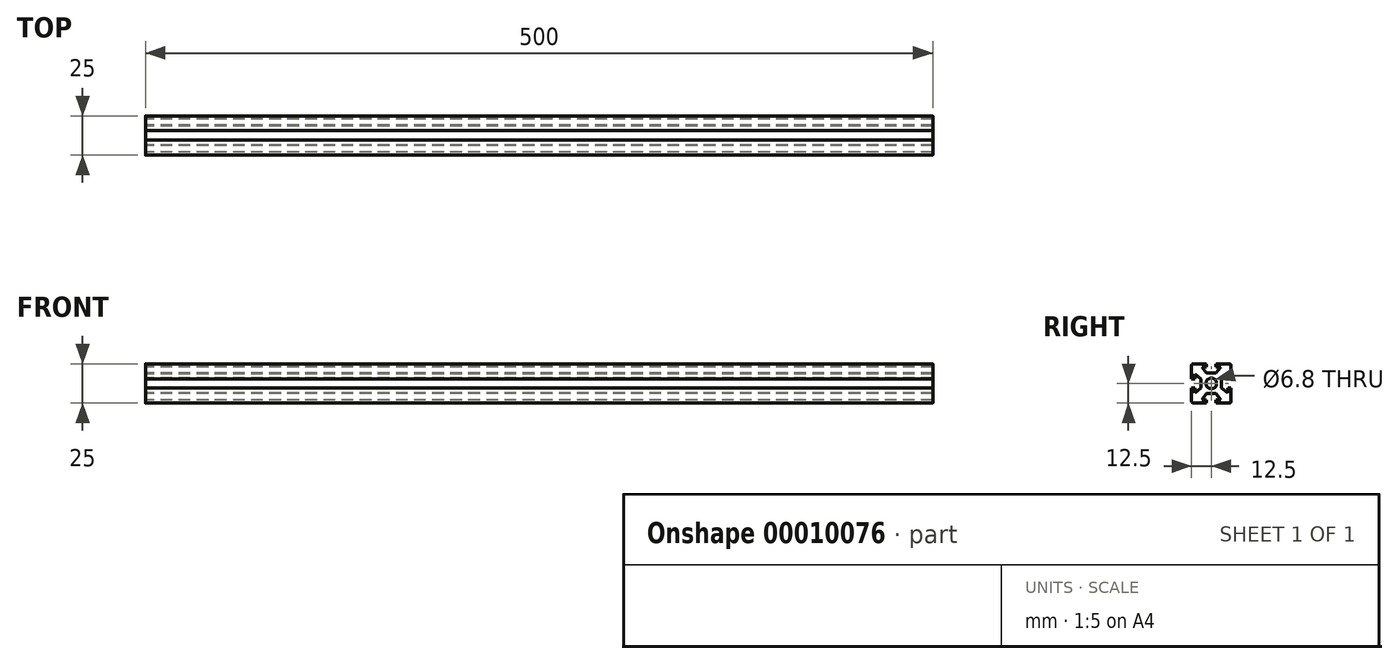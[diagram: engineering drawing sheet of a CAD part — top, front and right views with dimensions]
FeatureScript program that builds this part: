
annotation { "Feature Type Name" : "Feature", "Feature Type Description" : "" }
export const myFeature = defineFeature(function(context is Context, id is Id, definition is map)
    precondition{}
    {
        {
            var Q0;
            Q0=qCreatedBy(makeId("Right.planeOp"),FACE);
            var sketch = newSketch(context, id + "F0", { "sketchPlane" : qUnion([Q0])});
            skLineSegment(sketch, "E0", {"start": v(3, -12.5) * mm, "end": v(12.5, -12.5) * mm});
            skLineSegment(sketch, "E1", {"start": v(12.5, -12.5) * mm, "end": v(12.5, -3) * mm});
            skLineSegment(sketch, "E2", {"start": v(12.5, -3) * mm, "end": v(10.5, -3) * mm});
            skLineSegment(sketch, "E3", {"start": v(10.5, -3) * mm, "end": v(10.5, -6) * mm});
            skLineSegment(sketch, "E4", {"start": v(10.5, -6) * mm, "end": v(6.5, -3) * mm});
            skLineSegment(sketch, "E5", {"start": v(6.5, -3) * mm, "end": v(6.5, 3) * mm});
            skLineSegment(sketch, "E6", {"start": v(6.5, 3) * mm, "end": v(10.5, 6) * mm});
            skLineSegment(sketch, "E7", {"start": v(10.5, 6) * mm, "end": v(10.5, 3) * mm});
            skLineSegment(sketch, "E8", {"start": v(10.5, 3) * mm, "end": v(12.5, 3) * mm});
            skLineSegment(sketch, "E9", {"start": v(12.5, 3) * mm, "end": v(12.5, 12.5) * mm});
            skLineSegment(sketch, "E10", {"start": v(12.5, 12.5) * mm, "end": v(3, 12.5) * mm});
            skLineSegment(sketch, "E11", {"start": v(3, 12.5) * mm, "end": v(3, 10.5) * mm});
            skLineSegment(sketch, "E12", {"start": v(3, 10.5) * mm, "end": v(6, 10.5) * mm});
            skLineSegment(sketch, "E13", {"start": v(6, 10.5) * mm, "end": v(3, 6.5) * mm});
            skLineSegment(sketch, "E14", {"start": v(-3, 6.5) * mm, "end": v(-6, 10.5) * mm});
            skLineSegment(sketch, "E15", {"start": v(-6, 10.5) * mm, "end": v(-3, 10.5) * mm});
            skLineSegment(sketch, "E16", {"start": v(-3, 10.5) * mm, "end": v(-3, 12.5) * mm});
            skLineSegment(sketch, "E17", {"start": v(-3, 12.5) * mm, "end": v(-12.5, 12.5) * mm});
            skLineSegment(sketch, "E18", {"start": v(-12.5, 12.5) * mm, "end": v(-12.5, 3) * mm});
            skLineSegment(sketch, "E19", {"start": v(-12.5, 3) * mm, "end": v(-10.5, 3) * mm});
            skLineSegment(sketch, "E20", {"start": v(-10.5, 3) * mm, "end": v(-10.5, 6) * mm});
            skLineSegment(sketch, "E21", {"start": v(-10.5, 6) * mm, "end": v(-6.5, 3) * mm});
            skLineSegment(sketch, "E22", {"start": v(-6.5, 3) * mm, "end": v(-6.5, -3) * mm});
            skLineSegment(sketch, "E23", {"start": v(-6.5, -3) * mm, "end": v(-10.5, -6) * mm});
            skLineSegment(sketch, "E24", {"start": v(-10.5, -6) * mm, "end": v(-10.5, -3) * mm});
            skLineSegment(sketch, "E25", {"start": v(-10.5, -3) * mm, "end": v(-12.5, -3) * mm});
            skLineSegment(sketch, "E26", {"start": v(-12.5, -3) * mm, "end": v(-12.5, -12.5) * mm});
            skLineSegment(sketch, "E27", {"start": v(-12.5, -12.5) * mm, "end": v(-3, -12.5) * mm});
            skLineSegment(sketch, "E28", {"start": v(-3, -12.5) * mm, "end": v(-3, -10.5) * mm});
            skLineSegment(sketch, "E29", {"start": v(-3, -10.5) * mm, "end": v(-6, -10.5) * mm});
            skLineSegment(sketch, "E30", {"start": v(-6, -10.5) * mm, "end": v(-3, -6.5) * mm});
            skLineSegment(sketch, "E31", {"start": v(-3, -6.5) * mm, "end": v(3, -6.5) * mm});
            skLineSegment(sketch, "E32", {"start": v(3, -6.5) * mm, "end": v(6, -10.5) * mm});
            skLineSegment(sketch, "E33", {"start": v(6, -10.5) * mm, "end": v(3, -10.5) * mm});
            skLineSegment(sketch, "E34", {"start": v(3, -10.5) * mm, "end": v(3, -12.5) * mm});
            skLineSegment(sketch, "E35", {"start": v(3, 6.5) * mm, "end": v(-3, 6.5) * mm});
            skLineSegment(sketch, "E36", {"start": v(-12.5, -3) * mm, "end": v(-12.5, 3) * mm, "construction": true});
            skLineSegment(sketch, "E37", {"start": v(-3, 12.5) * mm, "end": v(3, 12.5) * mm, "construction": true});
            skLineSegment(sketch, "E38", {"start": v(12.5, 3) * mm, "end": v(12.5, -3) * mm, "construction": true});
            skLineSegment(sketch, "E39", {"start": v(3, -12.5) * mm, "end": v(-3, -12.5) * mm, "construction": true});
            skLineSegment(sketch, "E40", {"start": v(0, -12.5) * mm, "end": v(0, 12.5) * mm, "construction": true});
            skLineSegment(sketch, "E41", {"start": v(12.5, 0) * mm, "end": v(-12.5, 0) * mm, "construction": true});
            skCircle(sketch, "E42", {"center": v(0, 0) * mm, "radius": 3.4 * mm});
            skSolve(sketch);
        }
        {
            var Q0;
            Q0=makeQuery(id+"F0.imprint","IMPRINT",FACE,{"disambiguationData":[TD([[makeQuery(id+"F0.imprint","IMPRINT",EDGE,{"derivedFrom":sQuery(id+"F0.wireOp",EDGE,"E0")}),1.0]])]});
            extrude(context, id + "F1", {"entities" : qUnion([Q0]), "depth" : 500 * mm});
        }
        {
            var Q0;
            Q0=makeQuery(id+"F1.opExtrude","SWEPT_EDGE",EDGE,{"disambiguationData":[OSD([sQuery(id+"F0.wireOp",EDGE,"E0"),sQuery(id+"F0.wireOp",EDGE,"E1")])]});
            var Q1;
            Q1=makeQuery(id+"F1.opExtrude","SWEPT_EDGE",EDGE,{"disambiguationData":[OSD([sQuery(id+"F0.wireOp",EDGE,"E9"),sQuery(id+"F0.wireOp",EDGE,"E10")])]});
            var Q2;
            Q2=makeQuery(id+"F1.opExtrude","SWEPT_EDGE",EDGE,{"disambiguationData":[OSD([sQuery(id+"F0.wireOp",EDGE,"E26"),sQuery(id+"F0.wireOp",EDGE,"E27")])]});
            var Q3;
            Q3=makeQuery(id+"F1.opExtrude","SWEPT_EDGE",EDGE,{"disambiguationData":[OSD([sQuery(id+"F0.wireOp",EDGE,"E17"),sQuery(id+"F0.wireOp",EDGE,"E18")])]});
            fillet(context, id + "F2", {"entities" : qUnion([Q0, Q1, Q2, Q3]), "radius" : 1 * mm, "tangentPropagation" : true, "allowEdgeOverflow" : false});
        }
    });
